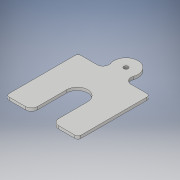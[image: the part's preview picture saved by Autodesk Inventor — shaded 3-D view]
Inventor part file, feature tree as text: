
AUTODESK INVENTOR PART (.ipt)
format: ipt  version: 2018 (Build 220112000, 112)  size: 135,680 bytes
history: native  units: in
note: dims shown in document units (in); Inventor stores cm internally (conversion verified against a paired STEP export)
features: extrude x1, sketch x1, fillet x1
ambient origin geometry x8: Origin, YZ Plane, XZ Plane, XY Plane, X Axis, Y Axis, Z Axis, Center Point
bodies: Solid1 (feature_tree)
feature tree (3):
  extrude  "Extrusion1"  Depth=1.0in TaperAngle=0.0deg
  sketch  "Sketch1"  dims[d0=0.091in d1=1.0in d2=0.0in]
  fillet  "Fillet2"  [1 undecoded]
note: 1 required parameter value undecoded (feature->parameter linkage not recoverable at this tier; creation-order binding heuristic only, values carry confidence <= 0.55)
